# Revit family: Faucet-Lavatory-KOHLER-PURIST-14402W_1
name_source: partatom
category: Plumbing Fixtures
revit_build: Autodesk Revit 2017 (Build: 20160225_1515(x64)
units: mm (PartAtom-declared; Revit-internal decimal feet)

## family parameters
Cut with Voids When Loaded = No
Host = Face
OmniClass Number = 23.31.11.00
OmniClass Title = Faucets
Part Type = Normal
Room Calculation Point = No
Round Connector Dimension = Use Diameter
Shared = No

## types (2) — shared parameters
ADA Compliant = No
Assembly Code = D2010
CW Connection = Yes
Cold Water Inlet = Cold Water Inlet
Date Modified = 03/12/2021
Default Elevation = 36"
Description = Single-lever monobloc basin mixer, smile handle
Drain Included = Yes
Finish = Kohler-Metal-CP-Polished_Chrome
Flow Rate = 2 GPM
HW Connection = Yes
Handle Clearance = 3"
Hot Water Inlet = Hot Water Inlet
Length = 5 1/2"
Manufacturer = KOHLER Co.
Master Format 2014 = 22 41 39
Master Format 2014 Name = Residential Faucets, Supplies, and Trim
Material = Premium Metal Construction
Pressure = 45.00 psi
Product Name = PURIST
Product Page URL = https://www.kohler.co.uk
Spout Reach = 5 1/2"
URL = https://www.kohler.co.uk
Vent Connection = No
Waste Connection = No
Waste Water Outlet = Waste Water Outlet
WaterSense Certified = No
Width = 2 1/4"

## per-type parameters (varying)
| type | Height | Model | Smile Lever Handle | Straight Lever Handle | Type |
| Smile Handle, CP- Polished Chrome | 7 15/16" | 14402W-4-CP | Yes | No | 1 |
| Straight Handle, CP- Polished Chrome | 7 3/4" | 14402W-4A-CP | No | Yes | 2 |

## geometry (parser evidence)
native form markers: Sweep x5
no freeform markers — native parametric forms only
